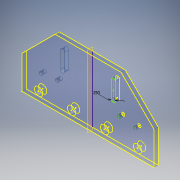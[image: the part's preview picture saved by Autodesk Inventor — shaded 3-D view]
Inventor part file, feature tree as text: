
AUTODESK INVENTOR PART (.ipt)
format: ipt  version: 2017 (Build 210142000, 142)  size: 188,928 bytes
history: native  units: in
note: dims shown in document units (in); Inventor stores cm internally (conversion verified against a paired STEP export)
features: sketch x4, projected_geometry x3, extrude x2, hole x2, mirror x2, pattern_linear x1, plane x1
ambient origin geometry x8: Origin, YZ Plane, XZ Plane, XY Plane, X Axis, Y Axis, Z Axis, Center Point
bodies: Solid1 (feature_tree)
feature tree (15):
  extrude  "Extrusion1"  Depth=2.0in
  hole  "Hole1"  [1 undecoded]
  pattern_linear  "Rectangular Pattern1"  Spacing1=8.0in  [1 undecoded]
  sketch  "Sketch3"  dims[d4=0.25in d5=0.0in]
  hole  "Hole2"  [1 undecoded]
  extrude  "Extrusion2"  Depth=0.25in
  sketch  "Sketch4"  dims[d6=0.5in d7=8.0in d8=4.0in d9=1.0in d10=0.5in d11=0.75in d12=0.375in d13=0.25in d14=0.5635in d15=1.0in d16=0.8108in d17=1.5748in d19=2.0in d20=0.25in d21=0.196in d22=0.5in d23=0.119in d24=0.25in d25=0.5635in d26=0.75in d27=0.8108in d28=0.25in d29=0.0in d30=0.0in]
  plane  "Work Plane1"
  mirror  "Mirror1"
  mirror  "Mirror2"
  sketch  "Sketch1"  dims[d0=2.0in d1=2.0in]
  sketch  "Sketch2"  dims[d2=2.0in d3=2.0in]
  projected_geometry  "Projected Loop1"
  projected_geometry  "Projected Loop2"
  projected_geometry  "Projected Loop3"
note: 3 required parameter values undecoded (feature->parameter linkage not recoverable at this tier; creation-order binding heuristic only, values carry confidence <= 0.55)
